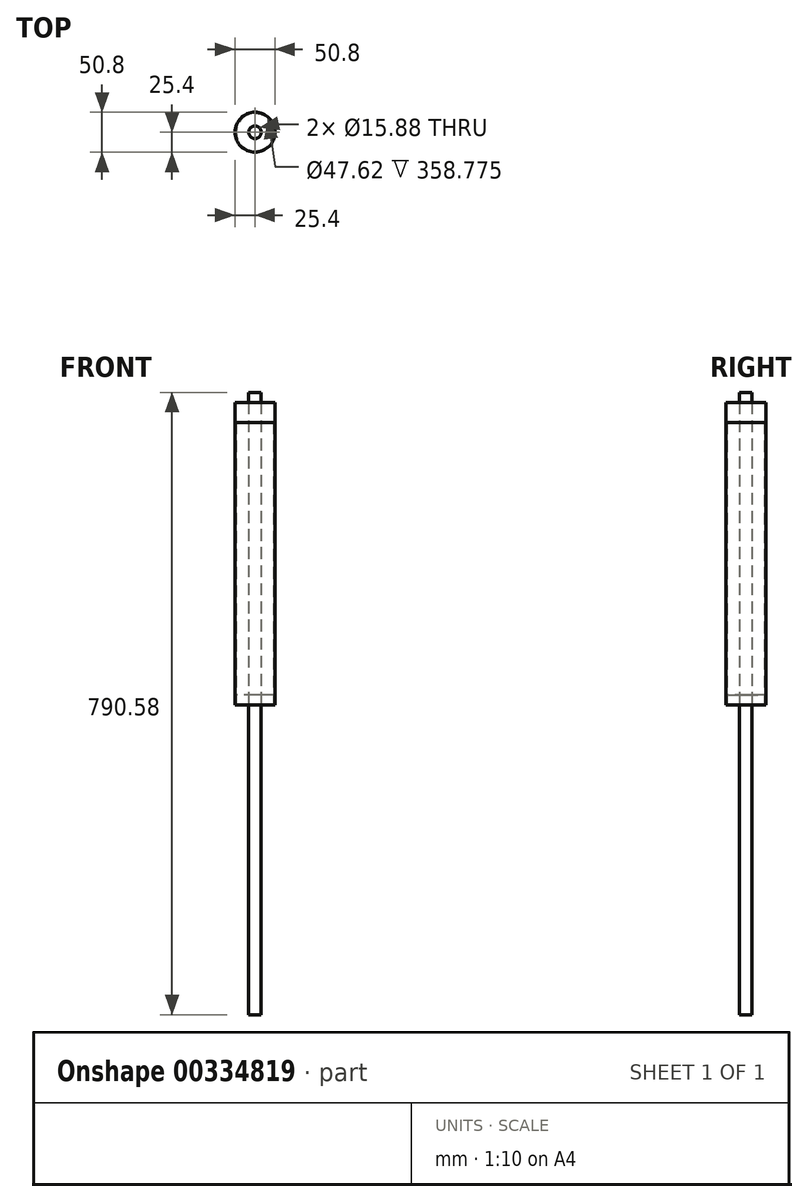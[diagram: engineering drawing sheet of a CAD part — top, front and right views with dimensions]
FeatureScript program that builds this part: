
annotation { "Feature Type Name" : "Feature", "Feature Type Description" : "" }
export const myFeature = defineFeature(function(context is Context, id is Id, definition is map)
    precondition{}
    {
        {
            var Q0;
            Q0=qCreatedBy(makeId("Top.planeOp"),FACE);
            var sketch = newSketch(context, id + "F0", { "sketchPlane" : qUnion([Q0])});
            skCircle(sketch, "E0", {"center": v(0, 0) * mm, "radius": 25.4 * mm});
            skCircle(sketch, "E1.0", {"center": v(0, 0) * mm, "radius": 23.81 * mm});
            skSolve(sketch);
        }
        {
            var Q0;
            Q0 = qSketchRegion(id + "F0", true);
            extrude(context, id + "F1", {"entities" : qUnion([Q0]), "depth" : 358.77 * mm});
        }
        {
            var Q0;
            Q0=makeQuery(id+"F1.opExtrude","CAP_FACE",FACE,{"disambiguationData":[OSD([sQuery(id+"F0.wireOp",EDGE,"E0"),sQuery(id+"F0.wireOp",EDGE,"E1.0")])],"isStart":false});
            var sketch = newSketch(context, id + "F2", { "sketchPlane" : qUnion([Q0])});
            skCircle(sketch, "E2.0", {"center": v(0, 0) * mm, "radius": 25.4 * mm});
            skCircle(sketch, "E3", {"center": v(0, 0) * mm, "radius": 7.94 * mm});
            skSolve(sketch);
        }
        {
            var Q0;
            Q0 = qSketchRegion(id + "F2", true);
            extrude(context, id + "F3", {"entities" : qUnion([Q0]), "depth" : 25.4 * mm});
        }
        {
            var Q0;
            Q0=qCreatedBy(makeId("Top.planeOp"),FACE);
            var sketch = newSketch(context, id + "F4", { "sketchPlane" : qUnion([Q0])});
            skCircle(sketch, "E4.0", {"center": v(0, 0) * mm, "radius": 23.81 * mm});
            skCircle(sketch, "E5.0", {"center": v(0, 0) * mm, "radius": 7.94 * mm});
            skSolve(sketch);
        }
        {
            var Q0;
            Q0 = qSketchRegion(id + "F4", true);
            extrude(context, id + "F5", {"entities" : qUnion([Q0]), "depth" : 12.7 * mm});
        }
        {
            var Q0;
            Q0=makeQuery(id+"F5.opExtrude","CAP_FACE",FACE,{"disambiguationData":[OSD([sQuery(id+"F4.wireOp",EDGE,"E4.0"),sQuery(id+"F4.wireOp",EDGE,"E5.0")])],"isStart":true});
            var sketch = newSketch(context, id + "F6", { "sketchPlane" : qUnion([Q0])});
            skCircle(sketch, "E6.0", {"center": v(0, 0) * mm, "radius": 7.94 * mm});
            skSolve(sketch);
        }
        {
            var Q0;
            Q0 = qSketchRegion(id + "F6", true);
            extrude(context, id + "F7", {"entities" : qUnion([Q0]), "oppositeDirection" : true, "depth" : 396.88 * mm});
        }
        {
            var Q0;
            Q0=makeQuery(id+"F7.opExtrude","CAP_FACE",FACE,{"disambiguationData":[OSD([sQuery(id+"F6.wireOp",EDGE,"E6.0")])],"isStart":true});
            var sketch = newSketch(context, id + "F8", { "sketchPlane" : qUnion([Q0])});
            skCircle(sketch, "E7.0", {"center": v(0, 0) * mm, "radius": 7.94 * mm});
            skSolve(sketch);
        }
        {
            var Q0;
            Q0 = qSketchRegion(id + "F8", true);
            extrude(context, id + "F9", {"entities" : qUnion([Q0]), "depth" : 393.7 * mm});
        }
    });
